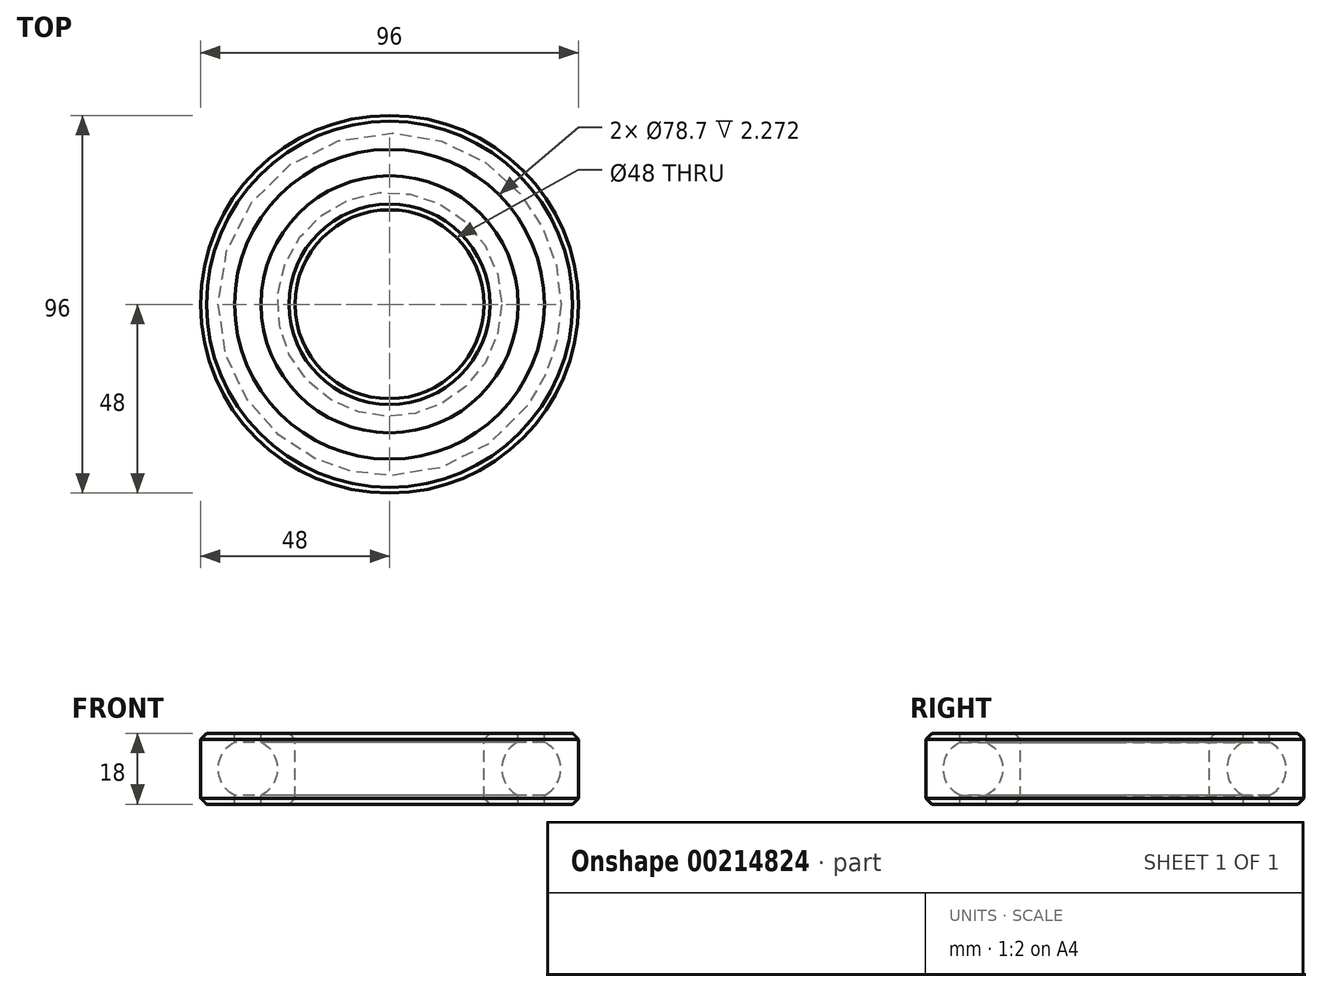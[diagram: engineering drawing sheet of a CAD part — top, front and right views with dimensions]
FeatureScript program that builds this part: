
annotation { "Feature Type Name" : "Feature", "Feature Type Description" : "" }
export const myFeature = defineFeature(function(context is Context, id is Id, definition is map)
    precondition{}
    {
        {
            var Q0;
            Q0=qCreatedBy(makeId("Front.planeOp"),FACE);
            var sketch = newSketch(context, id + "F0", { "sketchPlane" : qUnion([Q0])});
            skLineSegment(sketch, "E0", {"start": v(0, 36.3) * mm, "end": v(0, -40.62) * mm, "construction": true});
            skArc(sketch, "E1", {"start": v(-39.35, 6.73) * mm, "mid": v(-43.52, 0) * mm, "end": v(-39.35, -6.73) * mm});
            skLineSegment(sketch, "E2", {"start": v(-36, -14.48) * mm, "end": v(-36, 15.4) * mm, "construction": true});
            skLineSegment(sketch, "E3", {"start": v(-39.35, 9) * mm, "end": v(-48, 9) * mm});
            skLineSegment(sketch, "E4", {"start": v(-48, 9) * mm, "end": v(-48, -9) * mm});
            skLineSegment(sketch, "E5", {"start": v(-48, -9) * mm, "end": v(-39.35, -9) * mm});
            skLineSegment(sketch, "E6", {"start": v(-39.35, 9) * mm, "end": v(-39.35, 6.73) * mm});
            skLineSegment(sketch, "E7", {"start": v(-39.35, -6.73) * mm, "end": v(-39.35, -9) * mm});
            skCircle(sketch, "E8", {"center": v(-36, 0) * mm, "radius": 7.25 * mm, "construction": true});
            skLineSegment(sketch, "E9.MirrorCS", {"start": v(-32.65, 9) * mm, "end": v(-24, 9) * mm});
            skLineSegment(sketch, "E10.MirrorCS", {"start": v(-32.65, -6.73) * mm, "end": v(-32.65, -9) * mm});
            skArc(sketch, "E11.MirrorCS", {"start": v(-32.65, 6.73) * mm, "mid": v(-28.48, 0) * mm, "end": v(-32.65, -6.73) * mm});
            skLineSegment(sketch, "E12.MirrorCS", {"start": v(-24, -9) * mm, "end": v(-32.65, -9) * mm});
            skLineSegment(sketch, "E13.MirrorCS", {"start": v(-32.65, 9) * mm, "end": v(-32.65, 6.73) * mm});
            skLineSegment(sketch, "E14.MirrorCS", {"start": v(-24, 9) * mm, "end": v(-24, -9) * mm});
            skSolve(sketch);
        }
        {
            var Q0;
            Q0=makeQuery(id+"F0.imprint","IMPRINT",FACE,{"disambiguationData":[TD([[makeQuery(id+"F0.imprint","IMPRINT",EDGE,{"derivedFrom":sQuery(id+"F0.wireOp",EDGE,"E1")}),-1.0]])]});
            var Q1;
            Q1=makeQuery(id+"F0.imprint","IMPRINT",FACE,{"disambiguationData":[TD([[makeQuery(id+"F0.imprint","IMPRINT",EDGE,{"derivedFrom":sQuery(id+"F0.wireOp",EDGE,"E9.MirrorCS")}),-1.0]])]});
            var Q2;
            Q2=sQuery(id+"F0.wireOp",EDGE,"E0");
            revolve(context, id + "F1", {"entities" : qUnion([Q0, Q1]), "axis" : qUnion([Q2]), "revolveType" : RevolveType.FULL});
        }
        {
            var Q0;
            Q0=makeQuery(id+"F1.opRevolve","SWEPT_EDGE",EDGE,{"disambiguationData":[OSD([sQuery(id+"F0.wireOp",EDGE,"E3"),sQuery(id+"F0.wireOp",EDGE,"E4")])]});
            var Q1;
            Q1=makeQuery(id+"F1.opRevolve","SWEPT_EDGE",EDGE,{"disambiguationData":[OSD([sQuery(id+"F0.wireOp",EDGE,"E4"),sQuery(id+"F0.wireOp",EDGE,"E5")])]});
            var Q2;
            Q2=makeQuery(id+"F1.opRevolve","SWEPT_EDGE",EDGE,{"disambiguationData":[OSD([sQuery(id+"F0.wireOp",EDGE,"E9.MirrorCS"),sQuery(id+"F0.wireOp",EDGE,"E14.MirrorCS")])]});
            var Q3;
            Q3=makeQuery(id+"F1.opRevolve","SWEPT_EDGE",EDGE,{"disambiguationData":[OSD([sQuery(id+"F0.wireOp",EDGE,"E12.MirrorCS"),sQuery(id+"F0.wireOp",EDGE,"E14.MirrorCS")])]});
            chamfer(context, id + "F2", {"entities" : qUnion([Q0, Q1, Q2, Q3]), "width" : 1.5 * mm, "tangentPropagation" : true});
        }
        {
            var Q0;
            Q0=qCreatedBy(makeId("Front.planeOp"),FACE);
            var sketch = newSketch(context, id + "F3", { "sketchPlane" : qUnion([Q0])});
            skPoint(sketch, "E15.0", {"position": v(-36, 0) * mm});
            skArc(sketch, "E16", {"start": v(-36, -7.35) * mm, "mid": v(-28.65, 0) * mm, "end": v(-36, 7.35) * mm});
            skLineSegment(sketch, "E17.0", {"start": v(-36, -14.48) * mm, "end": v(-36, 15.4) * mm, "construction": true});
            skSolve(sketch);
        }
        {
            var Q0;
            Q0=sQuery(id+"F3.wireOp",EDGE,"E16");
            var Q1;
            Q1=sQuery(id+"F3.wireOp",EDGE,"E17.0");
            revolve(context, id + "F4", {"bodyType" : ToolBodyType.SURFACE, "surfaceEntities" : qUnion([Q0]), "axis" : qUnion([Q1]), "revolveType" : RevolveType.FULL});
        }
        {
            var Q0;
            Q0=makeQuery(id+"F4.opRevolve","SWEPT_BODY",BODY,{"disambiguationData":[OSD([sQuery(id+"F3.wireOp",EDGE,"E16")])]});
            var Q1;
            Q1=makeQuery(id+"F1.opRevolve","SWEPT_EDGE",EDGE,{"disambiguationData":[OSD([sQuery(id+"F0.wireOp",EDGE,"E9.MirrorCS"),sQuery(id+"F0.wireOp",EDGE,"E13.MirrorCS")])]});
            circularPattern(context, id + "F5", {"entities" : qUnion([Q0]), "axis" : qUnion([Q1]), "angle" : 360 * degree, "instanceCount" : 14, "equalSpace" : true});
        }
    });
